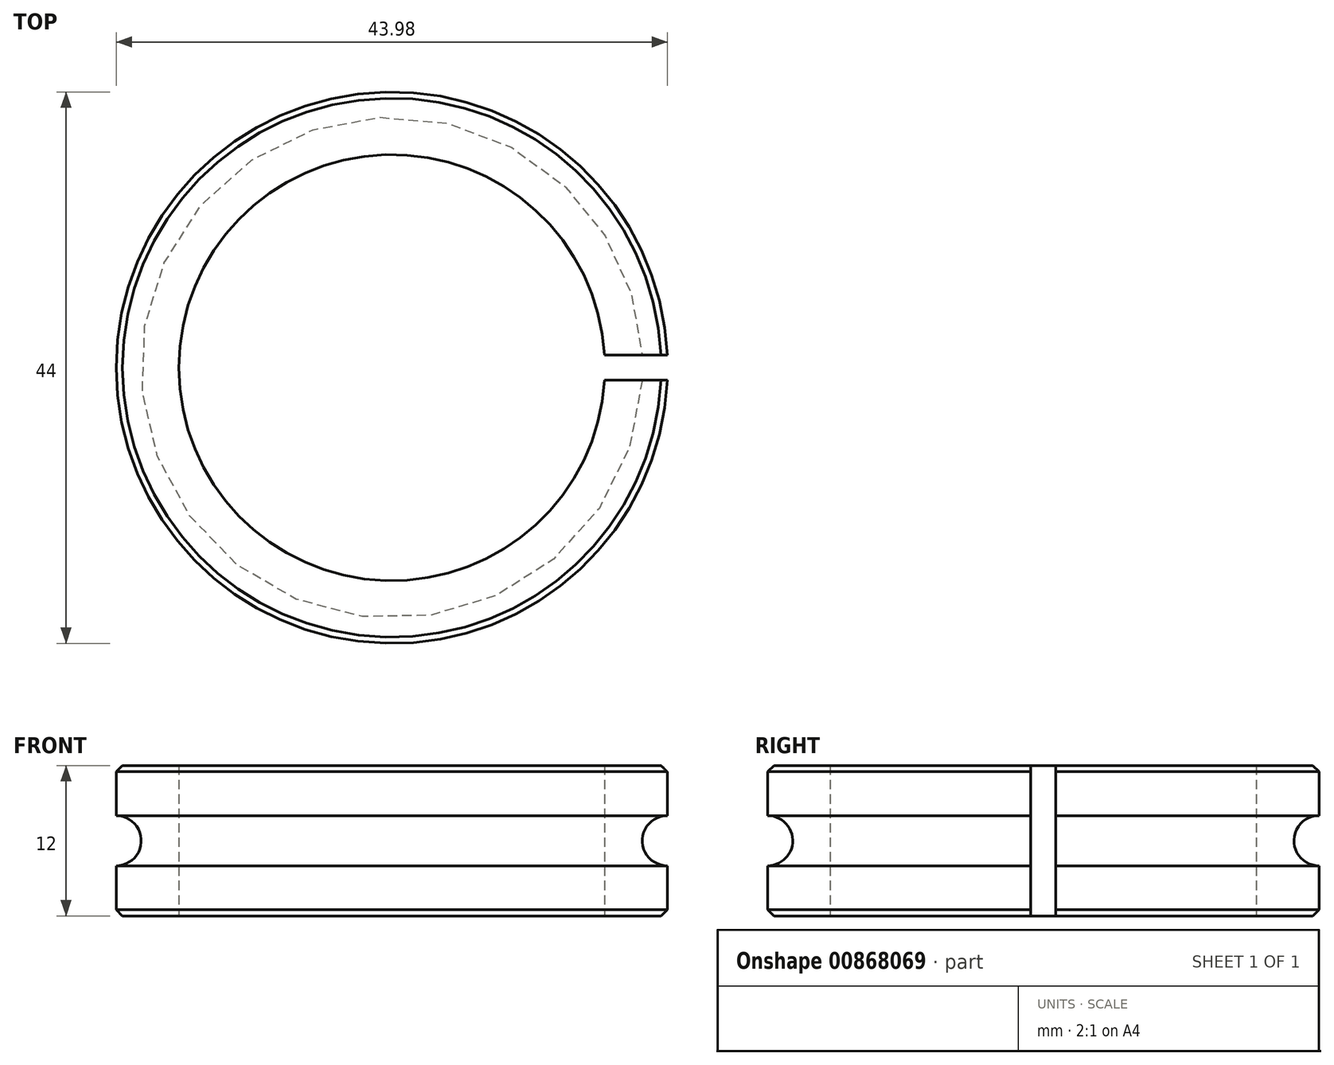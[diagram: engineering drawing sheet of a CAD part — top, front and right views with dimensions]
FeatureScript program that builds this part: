
annotation { "Feature Type Name" : "Feature", "Feature Type Description" : "" }
export const myFeature = defineFeature(function(context is Context, id is Id, definition is map)
    precondition{}
    {
        {
            var Q0;
            Q0=qCreatedBy(makeId("Front.planeOp"),FACE);
            var sketch = newSketch(context, id + "F0", { "sketchPlane" : qUnion([Q0])});
            skLineSegment(sketch, "E0", {"start": v(-17, 0) * mm, "end": v(-17, 6) * mm});
            skLineSegment(sketch, "E1", {"start": v(-17, 0) * mm, "end": v(-17, -6) * mm});
            skLineSegment(sketch, "E2", {"start": v(-17, -6) * mm, "end": v(-22, -6) * mm});
            skLineSegment(sketch, "E3", {"start": v(-22, -6) * mm, "end": v(-22, -2) * mm});
            skLineSegment(sketch, "E4", {"start": v(-22, 6) * mm, "end": v(-17, 6) * mm});
            skArc(sketch, "E5", {"start": v(-22, -2) * mm, "mid": v(-20, 0) * mm, "end": v(-22, 2) * mm});
            skLineSegment(sketch, "E6.trimOffspring", {"start": v(-22, 2) * mm, "end": v(-22, 6) * mm});
            skLineSegment(sketch, "E7", {"start": v(0, 0) * mm, "end": v(0, 7.08) * mm, "construction": true});
            skSolve(sketch);
        }
        {
            var Q0;
            Q0=makeQuery(id+"F0.imprint","IMPRINT",FACE,{"disambiguationData":[TD([[makeQuery(id+"F0.imprint","IMPRINT",EDGE,{"derivedFrom":sQuery(id+"F0.wireOp",EDGE,"E0")}),1.0]])]});
            var Q1;
            Q1=sQuery(id+"F0.wireOp",EDGE,"E7");
            revolve(context, id + "F1", {"surfaceOperationType" : NewSurfaceOperationType.NEW, "entities" : qUnion([Q0]), "axis" : qUnion([Q1]), "revolveType" : RevolveType.FULL});
        }
        {
            var Q0;
            Q0=qCreatedBy(makeId("Top.planeOp"),FACE);
            var sketch = newSketch(context, id + "F2", { "sketchPlane" : qUnion([Q0])});
            skLineSegment(sketch, "E8.bottom", {"start": v(25, 1) * mm, "end": v(15, 1) * mm});
            skLineSegment(sketch, "E8.top", {"start": v(25, -1) * mm, "end": v(15, -1) * mm});
            skLineSegment(sketch, "E8.left", {"start": v(25, 1) * mm, "end": v(25, -1) * mm});
            skLineSegment(sketch, "E8.right", {"start": v(15, 1) * mm, "end": v(15, -1) * mm});
            skPoint(sketch, "E8.middle", {"position": v(20, 0) * mm});
            skSolve(sketch);
        }
        {
            var Q0;
            Q0=makeQuery(id+"F2.imprint","IMPRINT",FACE,{"disambiguationData":[TD([[makeQuery(id+"F2.imprint","IMPRINT",EDGE,{"derivedFrom":sQuery(id+"F2.wireOp",EDGE,"E8.bottom")}),1.0]])]});
            extrude(context, id + "F3", {"entities" : qUnion([Q0]), "operationType" : NewBodyOperationType.REMOVE, "endBound" : BoundingType.SYMMETRIC, "oppositeDirection" : true, "depth" : 25 * mm, "offsetDistance" : 25 * mm});
        }
        {
            var Q0;
            Q0=makeQuery(id+"F1.opRevolve","SWEPT_EDGE",EDGE,{"disambiguationData":[OSD([sQuery(id+"F0.wireOp",EDGE,"E2"),sQuery(id+"F0.wireOp",EDGE,"E3")])]});
            var Q1;
            Q1=makeQuery(id+"F1.opRevolve","SWEPT_EDGE",EDGE,{"disambiguationData":[OSD([sQuery(id+"F0.wireOp",EDGE,"E4"),sQuery(id+"F0.wireOp",EDGE,"E6.trimOffspring")])]});
            chamfer(context, id + "F4", {"entities" : qUnion([Q0, Q1]), "width" : 0.5 * mm, "tangentPropagation" : true});
        }
    });
